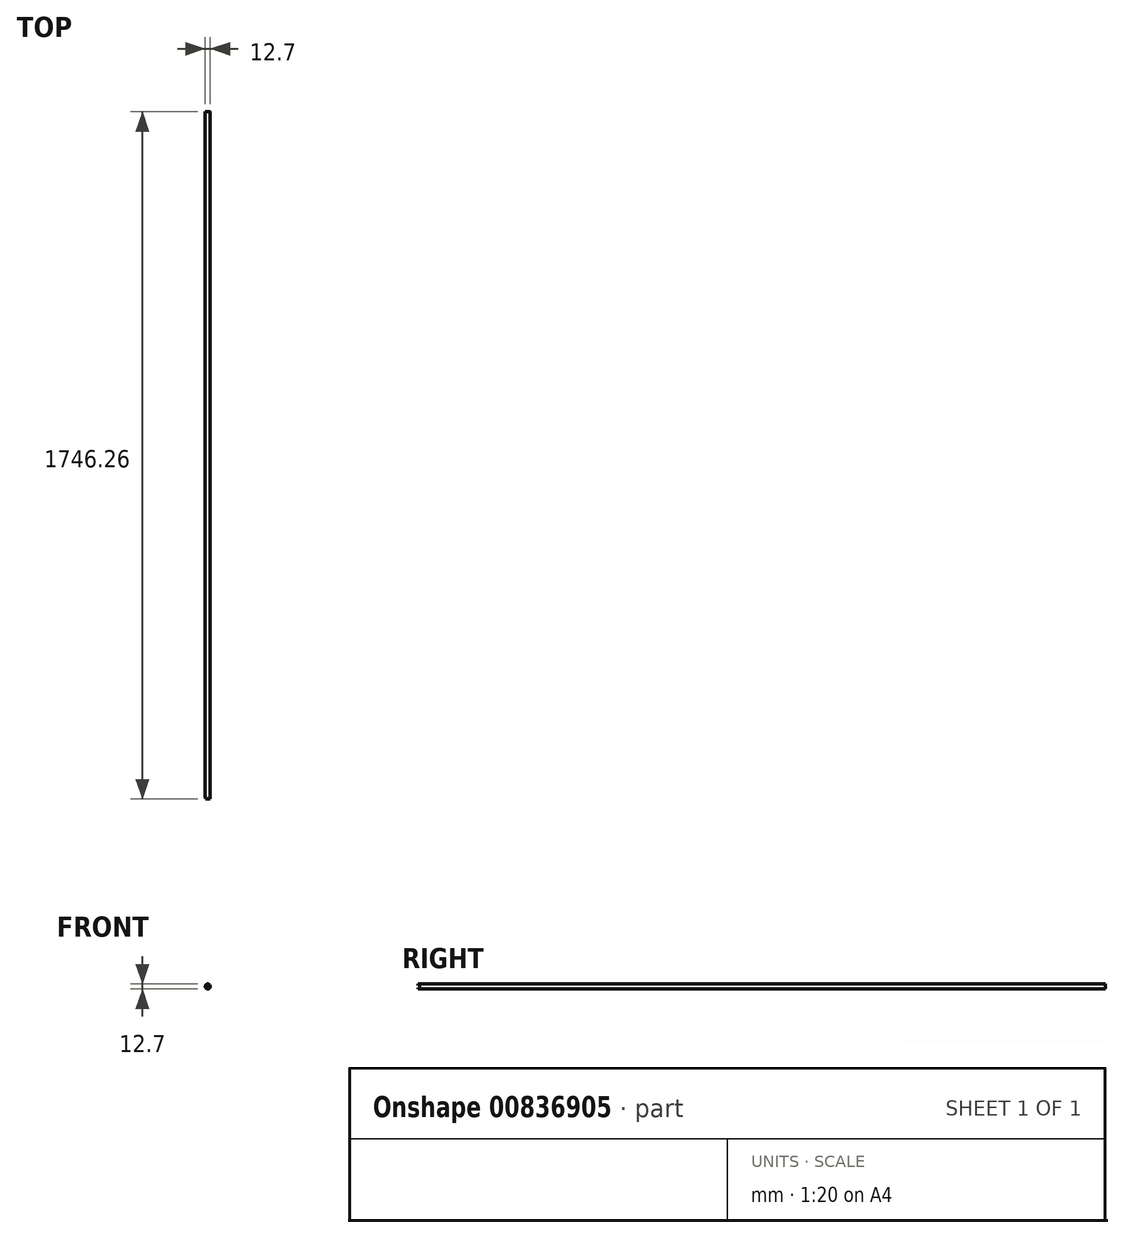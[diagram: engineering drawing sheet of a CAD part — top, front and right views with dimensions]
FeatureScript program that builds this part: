
annotation { "Feature Type Name" : "Feature", "Feature Type Description" : "" }
export const myFeature = defineFeature(function(context is Context, id is Id, definition is map)
    precondition{}
    {
        {
            var Q0;
            Q0=qCreatedBy(makeId("Front.planeOp"),FACE);
            var sketch = newSketch(context, id + "F0", { "sketchPlane" : qUnion([Q0])});
            skCircle(sketch, "E0", {"center": v(0, 0) * mm, "radius": 6.35 * mm});
            skSolve(sketch);
        }
        {
            var Q0;
            Q0 = qSketchRegion(id + "F0", true);
            extrude(context, id + "F1", {"entities" : qUnion([Q0]), "depth" : 1746.25 * mm, "offsetDistance" : 25.4 * mm, "symmetric" : true});
        }
        {
            var Q0;
            Q0=qCreatedBy(makeId("Right.planeOp"),FACE);
            var sketch = newSketch(context, id + "F2", { "sketchPlane" : qUnion([Q0])});
            skLineSegment(sketch, "E1", {"start": v(-884.48, 0) * mm, "end": v(-884.48, 0) * mm});
            skLineSegment(sketch, "E2", {"start": v(-884.48, 0) * mm, "end": v(-1.22, 0) * mm, "construction": true});
            skLineSegment(sketch, "E3.bottom", {"start": v(-877, 3.3) * mm, "end": v(-869.32, 3.3) * mm});
            skLineSegment(sketch, "E4.bottom", {"start": v(-875.97, -3.3) * mm, "end": v(-869.32, -3.3) * mm});
            skLineSegment(sketch, "E5", {"start": v(-875.97, -3.3) * mm, "end": v(-875.97, 3.3) * mm});
            skLineSegment(sketch, "E6", {"start": v(-869.32, -3.3) * mm, "end": v(-869.32, 3.3) * mm});
            skSolve(sketch);
        }
        {
            var Q0;
            Q0 = qSketchRegion(id + "F2", true);
            extrude(context, id + "F3", {"entities" : qUnion([Q0]), "operationType" : NewBodyOperationType.REMOVE, "oppositeDirection" : true, "depth" : 25.4 * mm, "offsetDistance" : 25.4 * mm, "symmetric" : true});
        }
    });
